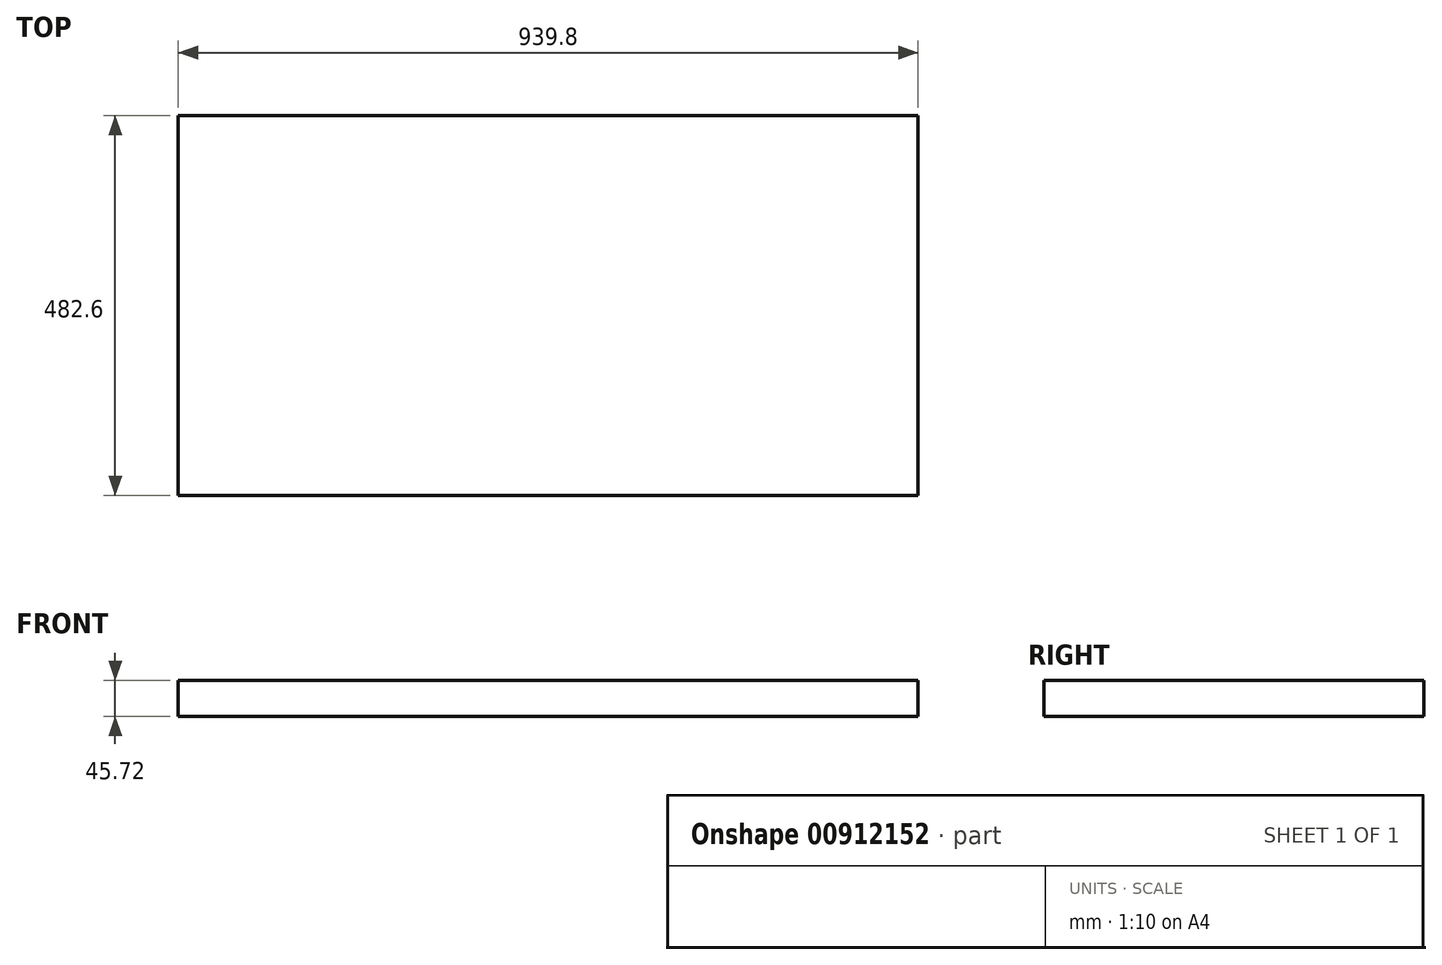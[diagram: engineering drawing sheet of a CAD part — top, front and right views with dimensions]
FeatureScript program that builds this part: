
annotation { "Feature Type Name" : "Feature", "Feature Type Description" : "" }
export const myFeature = defineFeature(function(context is Context, id is Id, definition is map)
    precondition{}
    {
        {
            var Q0;
            Q0=qCreatedBy(makeId("Top.planeOp"),FACE);
            var sketch = newSketch(context, id + "F0", { "sketchPlane" : qUnion([Q0])});
            skLineSegment(sketch, "E0.bottom", {"start": v(-134.31, 205.48) * mm, "end": v(805.49, 205.48) * mm});
            skLineSegment(sketch, "E0.top", {"start": v(-134.31, -277.12) * mm, "end": v(805.49, -277.12) * mm});
            skLineSegment(sketch, "E0.left", {"start": v(-134.31, 205.48) * mm, "end": v(-134.31, -277.12) * mm});
            skLineSegment(sketch, "E0.right", {"start": v(805.49, 205.48) * mm, "end": v(805.49, -277.12) * mm});
            skSolve(sketch);
        }
        {
            var Q0;
            Q0=makeQuery(id+"F0.imprint","IMPRINT",FACE,{"disambiguationData":[TD([[makeQuery(id+"F0.imprint","IMPRINT",EDGE,{"derivedFrom":sQuery(id+"F0.wireOp",EDGE,"E0.bottom")}),-1.0]])]});
            extrude(context, id + "F1", {"entities" : qUnion([Q0]), "depth" : 45.72 * mm, "offsetDistance" : 25.4 * mm});
        }
    });
